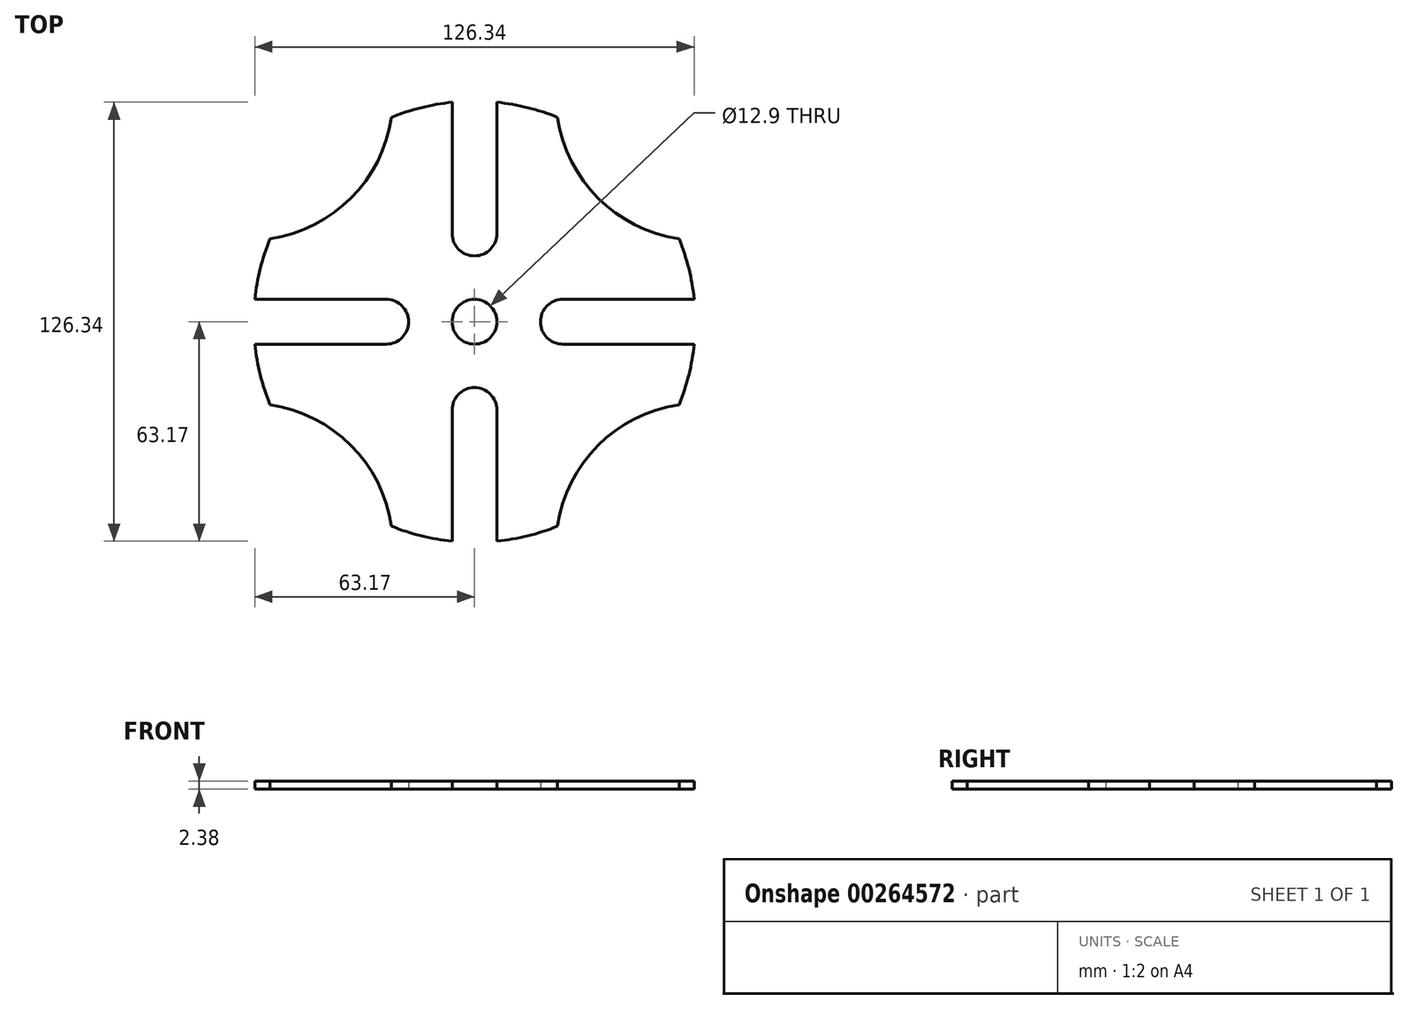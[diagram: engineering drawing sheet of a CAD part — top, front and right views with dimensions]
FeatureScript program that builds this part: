
annotation { "Feature Type Name" : "Feature", "Feature Type Description" : "" }
export const myFeature = defineFeature(function(context is Context, id is Id, definition is map)
    precondition{}
    {
        {
            var Q0;
            Q0=qCreatedBy(makeId("Top.planeOp"),FACE);
            var sketch = newSketch(context, id + "F0", { "sketchPlane" : qUnion([Q0])});
            skCircle(sketch, "E0", {"center": v(0, 0) * mm, "radius": 6.45 * mm});
            skArc(sketch, "E1", {"start": v(-58.85, 23.86) * mm, "mid": v(-61.63, 15.3) * mm, "end": v(-63.17, 6.45) * mm});
            skPoint(sketch, "E2", {"position": v(44.9, 44.9) * mm});
            skArc(sketch, "E3", {"start": v(-6.45, 25.4) * mm, "mid": v(0, 18.95) * mm, "end": v(6.45, 25.4) * mm});
            skArc(sketch, "E4", {"start": v(25.4, 6.45) * mm, "mid": v(18.95, 0) * mm, "end": v(25.4, -6.45) * mm});
            skArc(sketch, "E5", {"start": v(6.45, -25.4) * mm, "mid": v(0, -18.95) * mm, "end": v(-6.45, -25.4) * mm});
            skArc(sketch, "E6", {"start": v(-25.4, -6.45) * mm, "mid": v(-18.95, 0) * mm, "end": v(-25.4, 6.45) * mm});
            skLineSegment(sketch, "E7", {"start": v(-6.45, 63.17) * mm, "end": v(-6.45, 25.4) * mm});
            skLineSegment(sketch, "E8", {"start": v(6.45, 63.17) * mm, "end": v(6.45, 25.4) * mm});
            skLineSegment(sketch, "E9", {"start": v(63.17, 6.45) * mm, "end": v(25.4, 6.45) * mm});
            skLineSegment(sketch, "E10", {"start": v(63.17, -6.45) * mm, "end": v(25.4, -6.45) * mm});
            skLineSegment(sketch, "E11", {"start": v(-63.17, 6.45) * mm, "end": v(-25.4, 6.45) * mm});
            skLineSegment(sketch, "E12", {"start": v(-63.17, -6.45) * mm, "end": v(-25.4, -6.45) * mm});
            skLineSegment(sketch, "E13", {"start": v(-6.45, -63.17) * mm, "end": v(-6.45, -25.4) * mm});
            skLineSegment(sketch, "E14", {"start": v(6.45, -63.17) * mm, "end": v(6.45, -25.4) * mm});
            skArc(sketch, "E15", {"start": v(23.86, 58.85) * mm, "mid": v(35.57, 35.57) * mm, "end": v(58.85, 23.86) * mm});
            skArc(sketch, "E16.MirrorCS", {"start": v(58.85, 23.86) * mm, "mid": v(35.57, 35.57) * mm, "end": v(23.86, 58.85) * mm});
            skArc(sketch, "E17.MirrorCS", {"start": v(-23.86, 58.85) * mm, "mid": v(-35.57, 35.57) * mm, "end": v(-58.85, 23.86) * mm});
            skArc(sketch, "E18.MirrorCS", {"start": v(58.85, -23.86) * mm, "mid": v(35.57, -35.57) * mm, "end": v(23.86, -58.85) * mm});
            skArc(sketch, "E19.MirrorCS", {"start": v(-58.85, -23.86) * mm, "mid": v(-35.57, -35.57) * mm, "end": v(-23.86, -58.85) * mm});
            skArc(sketch, "E20.trimOffspring", {"start": v(-63.17, -6.45) * mm, "mid": v(-61.63, -15.3) * mm, "end": v(-58.85, -23.86) * mm});
            skArc(sketch, "E21.trimOffspring", {"start": v(-23.86, -58.85) * mm, "mid": v(-15.3, -61.63) * mm, "end": v(-6.45, -63.17) * mm});
            skArc(sketch, "E22.trimOffspring", {"start": v(58.85, -23.86) * mm, "mid": v(61.63, -15.3) * mm, "end": v(63.17, -6.45) * mm});
            skArc(sketch, "E23.trimOffspring", {"start": v(63.17, 6.45) * mm, "mid": v(61.63, 15.3) * mm, "end": v(58.85, 23.86) * mm});
            skArc(sketch, "E24.trimOffspring", {"start": v(23.86, 58.85) * mm, "mid": v(15.3, 61.63) * mm, "end": v(6.45, 63.17) * mm});
            skArc(sketch, "E25.trimOffspring", {"start": v(-6.45, 63.17) * mm, "mid": v(-15.3, 61.63) * mm, "end": v(-23.86, 58.85) * mm});
            skArc(sketch, "E26.trimOffspring", {"start": v(6.45, -63.17) * mm, "mid": v(15.3, -61.63) * mm, "end": v(23.86, -58.85) * mm});
            skPoint(sketch, "E27.MirrorCS.start.orphan", {"position": v(63.17, 6.45) * mm});
            skPoint(sketch, "E28.MirrorCS.end.orphan", {"position": v(58.85, 23.86) * mm});
            skLineSegment(sketch, "E29", {"start": v(25.4, 0) * mm, "end": v(74.7, 0) * mm});
            skLineSegment(sketch, "E30", {"start": v(63.17, 0) * mm, "end": v(78.29, 0) * mm});
            skLineSegment(sketch, "E31", {"start": v(78.29, 0) * mm, "end": v(64.93, -64.93) * mm});
            skSolve(sketch);
        }
        {
            var Q0;
            Q0 = qSketchRegion(id + "F0", true);
            extrude(context, id + "F1", {"entities" : qUnion([Q0]), "depth" : 2.38 * mm});
        }
    });
